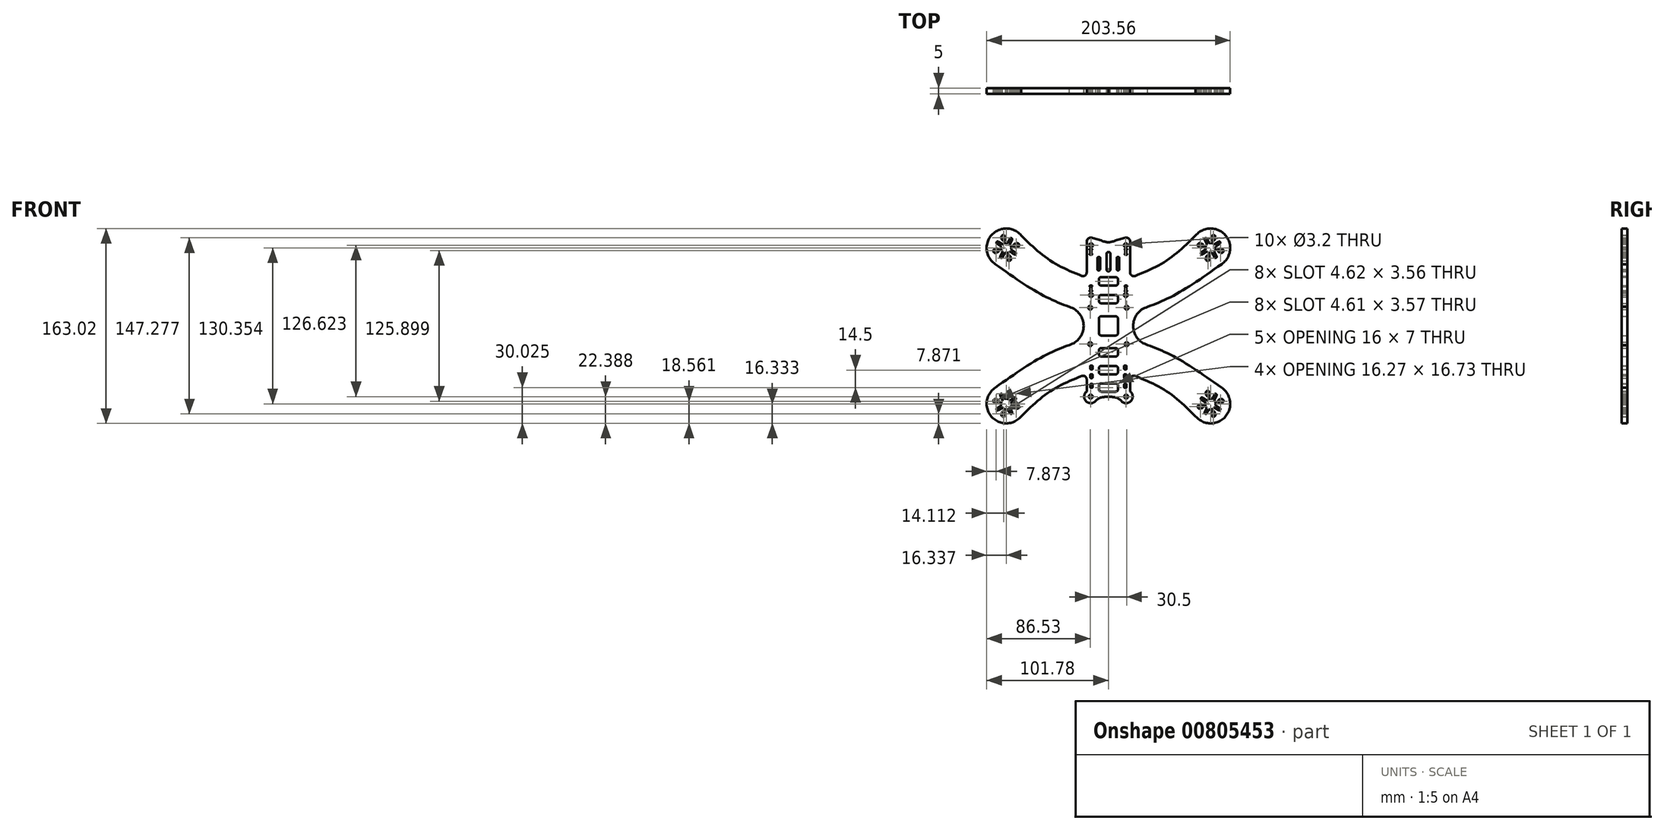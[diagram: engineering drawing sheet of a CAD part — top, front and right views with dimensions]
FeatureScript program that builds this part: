
annotation { "Feature Type Name" : "Feature", "Feature Type Description" : "" }
export const myFeature = defineFeature(function(context is Context, id is Id, definition is map)
    precondition{}
    {
        {
            var Q0;
            Q0=qCreatedBy(makeId("Front.planeOp"),FACE);
            var sketch = newSketch(context, id + "F0", { "sketchPlane" : qUnion([Q0])});
            skArc(sketch, "E0", {"start": v(-89.64, 66.06) * mm, "mid": v(-89.6, 64.08) * mm, "end": v(-88.66, 62.33) * mm});
            skLineSegment(sketch, "E1", {"start": v(0, 88.33) * mm, "end": v(0, -93.74) * mm, "construction": true});
            skPoint(sketch, "E2.startSnap0", {"position": v(-374.9, -63.32) * mm});
            skLineSegment(sketch, "E3.bottom", {"start": v(-6, 8) * mm, "end": v(6, 8) * mm});
            skLineSegment(sketch, "E3.top", {"start": v(-6, -8) * mm, "end": v(6, -8) * mm});
            skLineSegment(sketch, "E3.left", {"start": v(-8, 6) * mm, "end": v(-8, -6) * mm});
            skLineSegment(sketch, "E3.right", {"start": v(8, 6) * mm, "end": v(8, -6) * mm});
            skLineSegment(sketch, "E4", {"start": v(-85.44, 65.17) * mm, "end": v(85.13, -65.7) * mm, "construction": true});
            skCircle(sketch, "E5", {"center": v(85.13, -65.7) * mm, "radius": 4.25 * mm});
            skCircle(sketch, "E6.MirrorC", {"center": v(85.44, 65.17) * mm, "radius": 4.3 * mm});
            skCircle(sketch, "E7.MirrorC", {"center": v(-85.13, -65.7) * mm, "radius": 4.25 * mm});
            skLineSegment(sketch, "E8", {"start": v(-85.13, -65.7) * mm, "end": v(85.44, 65.17) * mm, "construction": true});
            skCircle(sketch, "E9", {"center": v(-15.25, 15.25) * mm, "radius": 1.6 * mm});
            skCircle(sketch, "E10.MirrorC", {"center": v(15.25, 15.25) * mm, "radius": 1.6 * mm});
            skCircle(sketch, "E11.MirrorC", {"center": v(-15.25, -15.25) * mm, "radius": 1.6 * mm});
            skCircle(sketch, "E12.MirrorC", {"center": v(15.25, -15.25) * mm, "radius": 1.6 * mm});
            skLineSegment(sketch, "E13", {"start": v(-42.21, 0) * mm, "end": v(44.56, 0) * mm, "construction": true});
            skArc(sketch, "E14", {"start": v(-72.93, 75.67) * mm, "mid": v(-97.56, 76.13) * mm, "end": v(-94.62, 51.67) * mm});
            skArc(sketch, "E15.MirrorC", {"start": v(72.93, 75.67) * mm, "mid": v(97.56, 76.13) * mm, "end": v(94.62, 51.67) * mm});
            skArc(sketch, "E16.MirrorC", {"start": v(-72.93, -75.67) * mm, "mid": v(-97.56, -76.13) * mm, "end": v(-94.62, -51.67) * mm});
            skArc(sketch, "E17.MirrorC", {"start": v(72.93, -75.67) * mm, "mid": v(97.56, -76.13) * mm, "end": v(94.62, -51.67) * mm});
            skLineSegment(sketch, "E18", {"start": v(-18.18, 44.65) * mm, "end": v(-18.18, 70.48) * mm});
            skLineSegment(sketch, "E19", {"start": v(-18.18, -44.65) * mm, "end": v(-18.18, -54.8) * mm});
            skArc(sketch, "E20", {"start": v(-18.18, -54.8) * mm, "mid": v(-18.83, -62.84) * mm, "end": v(-10.77, -62.88) * mm});
            skArc(sketch, "E21.MirrorC", {"start": v(18.18, -54.8) * mm, "mid": v(18.83, -62.84) * mm, "end": v(10.77, -62.88) * mm});
            skLineSegment(sketch, "E22.MirrorCS", {"start": v(18.18, -44.65) * mm, "end": v(18.18, -54.8) * mm});
            skFitSpline(sketch, "E23", {"points": [v(-72.93, 75.67) * mm, v(-47.95, 54.25) * mm, v(-18.18, 40.22) * mm], "startDerivative": vector(47.55, -46.42) * mm, "endDerivative": vector(61.29, -24.48) * mm});
            skFitSpline(sketch, "E24.MirrorCS", {"points": [v(72.93, 75.67) * mm, v(47.95, 54.25) * mm, v(18.18, 40.22) * mm], "startDerivative": vector(-47.55, -46.42) * mm, "endDerivative": vector(-61.29, -24.48) * mm});
            skFitSpline(sketch, "E25.MirrorCS", {"points": [v(-72.93, -75.67) * mm, v(-47.95, -54.25) * mm, v(-18.18, -40.22) * mm], "startDerivative": vector(47.55, 46.42) * mm, "endDerivative": vector(61.29, 24.48) * mm});
            skFitSpline(sketch, "E26.MirrorCS", {"points": [v(72.93, -75.67) * mm, v(47.95, -54.25) * mm, v(18.18, -40.22) * mm], "startDerivative": vector(-47.55, 46.42) * mm, "endDerivative": vector(-61.29, 24.48) * mm});
            skFitSpline(sketch, "E27", {"points": [v(-94.62, 51.67) * mm, v(-56.37, 26.47) * mm, v(-32.33, 15.78) * mm], "startDerivative": vector(71.34, -50.5) * mm, "endDerivative": vector(53.4, -20.59) * mm});
            skFitSpline(sketch, "E28.MirrorCS", {"points": [v(94.62, 51.67) * mm, v(56.37, 26.47) * mm, v(32.33, 15.78) * mm], "startDerivative": vector(-71.34, -50.5) * mm, "endDerivative": vector(-53.4, -20.59) * mm});
            skFitSpline(sketch, "E29.MirrorCS", {"points": [v(-94.62, -51.67) * mm, v(-56.37, -26.47) * mm, v(-32.33, -15.78) * mm], "startDerivative": vector(71.34, 50.5) * mm, "endDerivative": vector(53.4, 20.59) * mm});
            skFitSpline(sketch, "E30.MirrorCS", {"points": [v(94.62, -51.67) * mm, v(56.37, -26.47) * mm, v(32.33, -15.78) * mm], "startDerivative": vector(-71.34, 50.5) * mm, "endDerivative": vector(-53.4, 20.59) * mm});
            skPoint(sketch, "E31.orphan", {"position": v(-18.18, -38.8) * mm});
            skPoint(sketch, "E32.orphan", {"position": v(18.18, -38.8) * mm});
            skArc(sketch, "E33", {"start": v(-32.71, -15.93) * mm, "mid": v(-20.68, 0) * mm, "end": v(-32.71, 15.93) * mm});
            skArc(sketch, "E34.MirrorCS", {"start": v(32.71, -15.93) * mm, "mid": v(20.68, 0) * mm, "end": v(32.71, 15.93) * mm});
            skFitSpline(sketch, "E35", {"points": [v(-10.77, -62.88) * mm, v(-7.02, -60.12) * mm, v(0, -59.29) * mm], "startDerivative": vector(7.83, 7.8) * mm, "endDerivative": vector(14.08, 0.15) * mm});
            skFitSpline(sketch, "E36.MirrorCS", {"points": [v(10.77, -62.88) * mm, v(7.02, -60.12) * mm, v(0, -59.29) * mm], "startDerivative": vector(-7.83, 7.8) * mm, "endDerivative": vector(-14.08, 0.15) * mm});
            skPoint(sketch, "E37.orphan", {"position": v(-9.3, -59.45) * mm});
            skPoint(sketch, "E38.orphan", {"position": v(9.3, -59.45) * mm});
            skCircle(sketch, "E39", {"center": v(-14.78, -59.12) * mm, "radius": 1.6 * mm});
            skCircle(sketch, "E40.MirrorC", {"center": v(14.78, -59.12) * mm, "radius": 1.6 * mm});
            skCircle(sketch, "E41", {"center": v(-14.5, 25.75) * mm, "radius": 1.6 * mm});
            skCircle(sketch, "E42", {"center": v(-14.5, 67.5) * mm, "radius": 1.6 * mm});
            skCircle(sketch, "E43.MirrorC", {"center": v(14.5, 67.5) * mm, "radius": 1.6 * mm});
            skCircle(sketch, "E44.MirrorC", {"center": v(14.5, 25.75) * mm, "radius": 1.6 * mm});
            skArc(sketch, "E45.filletArc", {"start": v(-22.3, 41.86) * mm, "mid": v(-19.5, 42.16) * mm, "end": v(-18.18, 44.65) * mm});
            skPoint(sketch, "E46.newPointA", {"position": v(18.84, 40.22) * mm});
            skArc(sketch, "E47.filletArc", {"start": v(22.3, -41.86) * mm, "mid": v(19.5, -42.16) * mm, "end": v(18.18, -44.65) * mm});
            skArc(sketch, "E48.filletArc", {"start": v(-18.18, -44.65) * mm, "mid": v(-19.5, -42.16) * mm, "end": v(-22.3, -41.86) * mm});
            skLineSegment(sketch, "E49.MirrorCS", {"start": v(18.18, 44.65) * mm, "end": v(18.18, 70.48) * mm});
            skArc(sketch, "E50.MirrorCS", {"start": v(22.3, 41.86) * mm, "mid": v(19.5, 42.16) * mm, "end": v(18.18, 44.65) * mm});
            skPoint(sketch, "E51.orphan", {"position": v(-18.18, 74.02) * mm});
            skPoint(sketch, "E52.orphan", {"position": v(18.18, 74.02) * mm});
            skFitSpline(sketch, "E53", {"points": [v(-18.18, 71.17) * mm, v(-15.57, 73.68) * mm, v(-3.04, 70.45) * mm, v(0, 70.12) * mm], "startDerivative": vector(6.13, 13.03) * mm, "endDerivative": vector(9.34, 0.51) * mm});
            skArc(sketch, "E54.filletArc", {"start": v(-17.84, 71.88) * mm, "mid": v(-18.1, 71.2) * mm, "end": v(-18.18, 70.48) * mm});
            skFitSpline(sketch, "E55.MirrorCS", {"points": [v(18.18, 71.17) * mm, v(15.57, 73.68) * mm, v(3.04, 70.45) * mm, v(0, 70.12) * mm], "startDerivative": vector(-6.13, 13.03) * mm, "endDerivative": vector(-9.34, 0.51) * mm});
            skArc(sketch, "E56.MirrorCS", {"start": v(17.84, 71.88) * mm, "mid": v(18.1, 71.2) * mm, "end": v(18.18, 70.48) * mm});
            skPoint(sketch, "E57.visualSharp", {"position": v(-8, 8) * mm});
            skArc(sketch, "E57.filletArc", {"start": v(-6, 8) * mm, "mid": v(-7.41, 7.41) * mm, "end": v(-8, 6) * mm});
            skPoint(sketch, "E58.visualSharp", {"position": v(8, 8) * mm});
            skArc(sketch, "E58.filletArc", {"start": v(8, 6) * mm, "mid": v(7.41, 7.41) * mm, "end": v(6, 8) * mm});
            skPoint(sketch, "E59.visualSharp", {"position": v(8, -8) * mm});
            skArc(sketch, "E59.filletArc", {"start": v(6, -8) * mm, "mid": v(7.41, -7.41) * mm, "end": v(8, -6) * mm});
            skPoint(sketch, "E60.visualSharp", {"position": v(-8, -8) * mm});
            skArc(sketch, "E60.filletArc", {"start": v(-8, -6) * mm, "mid": v(-7.41, -7.41) * mm, "end": v(-6, -8) * mm});
            skLineSegment(sketch, "E61.bottom", {"start": v(-6, -18.58) * mm, "end": v(6, -18.58) * mm});
            skLineSegment(sketch, "E61.top", {"start": v(-6, -25.58) * mm, "end": v(6, -25.58) * mm});
            skLineSegment(sketch, "E61.left", {"start": v(-8, -20.58) * mm, "end": v(-8, -23.58) * mm});
            skLineSegment(sketch, "E61.right", {"start": v(8, -20.58) * mm, "end": v(8, -23.58) * mm});
            skPoint(sketch, "E62.visualSharp", {"position": v(-8, -18.58) * mm});
            skArc(sketch, "E62.filletArc", {"start": v(-6, -18.58) * mm, "mid": v(-7.41, -19.17) * mm, "end": v(-8, -20.58) * mm});
            skPoint(sketch, "E63.visualSharp", {"position": v(8, -18.58) * mm});
            skArc(sketch, "E63.filletArc", {"start": v(8, -20.58) * mm, "mid": v(7.41, -19.17) * mm, "end": v(6, -18.58) * mm});
            skPoint(sketch, "E64.visualSharp", {"position": v(8, -25.58) * mm});
            skArc(sketch, "E64.filletArc", {"start": v(6, -25.58) * mm, "mid": v(7.41, -25) * mm, "end": v(8, -23.58) * mm});
            skPoint(sketch, "E65.visualSharp", {"position": v(-8, -25.58) * mm});
            skArc(sketch, "E65.filletArc", {"start": v(-8, -23.58) * mm, "mid": v(-7.41, -25) * mm, "end": v(-6, -25.58) * mm});
            skLineSegment(sketch, "E66.bottom", {"start": v(-6, -33.49) * mm, "end": v(6, -33.49) * mm});
            skLineSegment(sketch, "E66.top", {"start": v(-6, -40.49) * mm, "end": v(6, -40.49) * mm});
            skLineSegment(sketch, "E66.left", {"start": v(-8, -35.49) * mm, "end": v(-8, -38.49) * mm});
            skLineSegment(sketch, "E66.right", {"start": v(8, -35.49) * mm, "end": v(8, -38.49) * mm});
            skPoint(sketch, "E67.visualSharp", {"position": v(-8, -33.49) * mm});
            skArc(sketch, "E67.filletArc", {"start": v(-6, -33.49) * mm, "mid": v(-7.41, -34.07) * mm, "end": v(-8, -35.49) * mm});
            skPoint(sketch, "E68.visualSharp", {"position": v(8, -33.49) * mm});
            skArc(sketch, "E68.filletArc", {"start": v(8, -35.49) * mm, "mid": v(7.41, -34.07) * mm, "end": v(6, -33.49) * mm});
            skPoint(sketch, "E69.visualSharp", {"position": v(8, -40.49) * mm});
            skArc(sketch, "E69.filletArc", {"start": v(6, -40.49) * mm, "mid": v(7.41, -39.9) * mm, "end": v(8, -38.49) * mm});
            skPoint(sketch, "E70.visualSharp", {"position": v(-8, -40.49) * mm});
            skArc(sketch, "E70.filletArc", {"start": v(-8, -38.49) * mm, "mid": v(-7.41, -39.9) * mm, "end": v(-6, -40.49) * mm});
            skLineSegment(sketch, "E71.bottom", {"start": v(-6, -47.99) * mm, "end": v(6, -47.99) * mm});
            skLineSegment(sketch, "E71.top", {"start": v(-6, -54.99) * mm, "end": v(6, -54.99) * mm});
            skLineSegment(sketch, "E71.left", {"start": v(-8, -49.99) * mm, "end": v(-8, -52.99) * mm});
            skLineSegment(sketch, "E71.right", {"start": v(8, -49.99) * mm, "end": v(8, -52.99) * mm});
            skPoint(sketch, "E72.visualSharp", {"position": v(-8, -47.99) * mm});
            skArc(sketch, "E72.filletArc", {"start": v(-6, -47.99) * mm, "mid": v(-7.41, -48.57) * mm, "end": v(-8, -49.99) * mm});
            skPoint(sketch, "E73.visualSharp", {"position": v(8, -47.99) * mm});
            skArc(sketch, "E73.filletArc", {"start": v(8, -49.99) * mm, "mid": v(7.41, -48.57) * mm, "end": v(6, -47.99) * mm});
            skPoint(sketch, "E74.visualSharp", {"position": v(8, -54.99) * mm});
            skArc(sketch, "E74.filletArc", {"start": v(6, -54.99) * mm, "mid": v(7.41, -54.4) * mm, "end": v(8, -52.99) * mm});
            skPoint(sketch, "E75.visualSharp", {"position": v(-8, -54.99) * mm});
            skArc(sketch, "E75.filletArc", {"start": v(-8, -52.99) * mm, "mid": v(-7.41, -54.4) * mm, "end": v(-6, -54.99) * mm});
            skLineSegment(sketch, "E76.bottom", {"start": v(-6, 25.92) * mm, "end": v(6, 25.92) * mm});
            skLineSegment(sketch, "E76.top", {"start": v(-6, 18.92) * mm, "end": v(6, 18.92) * mm});
            skLineSegment(sketch, "E76.left", {"start": v(-8, 23.92) * mm, "end": v(-8, 20.92) * mm});
            skLineSegment(sketch, "E76.right", {"start": v(8, 23.92) * mm, "end": v(8, 20.92) * mm});
            skPoint(sketch, "E77.visualSharp", {"position": v(-8, 25.92) * mm});
            skArc(sketch, "E77.filletArc", {"start": v(-6, 25.92) * mm, "mid": v(-7.41, 25.33) * mm, "end": v(-8, 23.92) * mm});
            skPoint(sketch, "E78.visualSharp", {"position": v(8, 25.92) * mm});
            skArc(sketch, "E78.filletArc", {"start": v(8, 23.92) * mm, "mid": v(7.41, 25.33) * mm, "end": v(6, 25.92) * mm});
            skPoint(sketch, "E79.visualSharp", {"position": v(8, 18.92) * mm});
            skArc(sketch, "E79.filletArc", {"start": v(6, 18.92) * mm, "mid": v(7.41, 19.5) * mm, "end": v(8, 20.92) * mm});
            skPoint(sketch, "E80.visualSharp", {"position": v(-8, 18.92) * mm});
            skArc(sketch, "E80.filletArc", {"start": v(-8, 20.92) * mm, "mid": v(-7.41, 19.5) * mm, "end": v(-6, 18.92) * mm});
            skLineSegment(sketch, "E81.bottom", {"start": v(-6, 40.78) * mm, "end": v(6, 40.78) * mm});
            skLineSegment(sketch, "E81.top", {"start": v(-6, 33.78) * mm, "end": v(6, 33.78) * mm});
            skLineSegment(sketch, "E81.left", {"start": v(-8, 38.78) * mm, "end": v(-8, 35.78) * mm});
            skLineSegment(sketch, "E81.right", {"start": v(8, 38.78) * mm, "end": v(8, 35.78) * mm});
            skPoint(sketch, "E82.visualSharp", {"position": v(-8, 40.78) * mm});
            skArc(sketch, "E82.filletArc", {"start": v(-6, 40.78) * mm, "mid": v(-7.41, 40.2) * mm, "end": v(-8, 38.78) * mm});
            skPoint(sketch, "E83.visualSharp", {"position": v(8, 40.78) * mm});
            skArc(sketch, "E83.filletArc", {"start": v(8, 38.78) * mm, "mid": v(7.41, 40.2) * mm, "end": v(6, 40.78) * mm});
            skPoint(sketch, "E84.visualSharp", {"position": v(8, 33.78) * mm});
            skArc(sketch, "E84.filletArc", {"start": v(6, 33.78) * mm, "mid": v(7.41, 34.37) * mm, "end": v(8, 35.78) * mm});
            skPoint(sketch, "E85.visualSharp", {"position": v(-8, 33.78) * mm});
            skArc(sketch, "E85.filletArc", {"start": v(-8, 35.78) * mm, "mid": v(-7.41, 34.37) * mm, "end": v(-6, 33.78) * mm});
            skLineSegment(sketch, "E86.bottom", {"start": v(-14.65, -33.17) * mm, "end": v(-13.65, -33.17) * mm});
            skLineSegment(sketch, "E86.top", {"start": v(-14.65, -36.37) * mm, "end": v(-13.65, -36.37) * mm});
            skLineSegment(sketch, "E86.left", {"start": v(-15.15, -33.67) * mm, "end": v(-15.15, -35.87) * mm});
            skLineSegment(sketch, "E86.right", {"start": v(-13.15, -33.67) * mm, "end": v(-13.15, -35.87) * mm});
            skPoint(sketch, "E87.visualSharp", {"position": v(-15.15, -33.17) * mm});
            skArc(sketch, "E87.filletArc", {"start": v(-14.65, -33.17) * mm, "mid": v(-15, -33.31) * mm, "end": v(-15.15, -33.67) * mm});
            skPoint(sketch, "E88.visualSharp", {"position": v(-13.15, -33.17) * mm});
            skArc(sketch, "E88.filletArc", {"start": v(-13.15, -33.67) * mm, "mid": v(-13.3, -33.31) * mm, "end": v(-13.65, -33.17) * mm});
            skPoint(sketch, "E89.visualSharp", {"position": v(-15.15, -36.37) * mm});
            skArc(sketch, "E89.filletArc", {"start": v(-15.15, -35.87) * mm, "mid": v(-15, -36.22) * mm, "end": v(-14.65, -36.37) * mm});
            skPoint(sketch, "E90.visualSharp", {"position": v(-13.15, -36.37) * mm});
            skArc(sketch, "E90.filletArc", {"start": v(-13.65, -36.37) * mm, "mid": v(-13.3, -36.22) * mm, "end": v(-13.15, -35.87) * mm});
            skLineSegment(sketch, "E91.bottom", {"start": v(-14.65, -40.37) * mm, "end": v(-13.65, -40.37) * mm});
            skLineSegment(sketch, "E91.top", {"start": v(-14.65, -43.57) * mm, "end": v(-13.65, -43.57) * mm});
            skLineSegment(sketch, "E91.left", {"start": v(-15.15, -40.87) * mm, "end": v(-15.15, -43.07) * mm});
            skLineSegment(sketch, "E91.right", {"start": v(-13.15, -40.87) * mm, "end": v(-13.15, -43.07) * mm});
            skPoint(sketch, "E92.visualSharp", {"position": v(-15.15, -40.37) * mm});
            skArc(sketch, "E92.filletArc", {"start": v(-14.65, -40.37) * mm, "mid": v(-15, -40.51) * mm, "end": v(-15.15, -40.87) * mm});
            skPoint(sketch, "E93.visualSharp", {"position": v(-13.15, -40.37) * mm});
            skArc(sketch, "E93.filletArc", {"start": v(-13.15, -40.87) * mm, "mid": v(-13.3, -40.51) * mm, "end": v(-13.65, -40.37) * mm});
            skPoint(sketch, "E94.visualSharp", {"position": v(-13.15, -43.57) * mm});
            skArc(sketch, "E94.filletArc", {"start": v(-13.65, -43.57) * mm, "mid": v(-13.3, -43.42) * mm, "end": v(-13.15, -43.07) * mm});
            skPoint(sketch, "E95.visualSharp", {"position": v(-15.15, -43.57) * mm});
            skArc(sketch, "E95.filletArc", {"start": v(-15.15, -43.07) * mm, "mid": v(-15, -43.42) * mm, "end": v(-14.65, -43.57) * mm});
            skLineSegment(sketch, "E96.bottom", {"start": v(-14.65, -48.57) * mm, "end": v(-13.65, -48.57) * mm});
            skLineSegment(sketch, "E96.top", {"start": v(-14.65, -51.77) * mm, "end": v(-13.65, -51.77) * mm});
            skLineSegment(sketch, "E96.left", {"start": v(-15.15, -49.07) * mm, "end": v(-15.15, -51.27) * mm});
            skLineSegment(sketch, "E96.right", {"start": v(-13.15, -49.07) * mm, "end": v(-13.15, -51.27) * mm});
            skPoint(sketch, "E97.visualSharp", {"position": v(-15.15, -48.57) * mm});
            skArc(sketch, "E97.filletArc", {"start": v(-14.65, -48.57) * mm, "mid": v(-15, -48.71) * mm, "end": v(-15.15, -49.07) * mm});
            skPoint(sketch, "E98.visualSharp", {"position": v(-13.15, -48.57) * mm});
            skArc(sketch, "E98.filletArc", {"start": v(-13.15, -49.07) * mm, "mid": v(-13.3, -48.71) * mm, "end": v(-13.65, -48.57) * mm});
            skPoint(sketch, "E99.visualSharp", {"position": v(-13.15, -51.77) * mm});
            skArc(sketch, "E99.filletArc", {"start": v(-13.65, -51.77) * mm, "mid": v(-13.3, -51.62) * mm, "end": v(-13.15, -51.27) * mm});
            skPoint(sketch, "E100.visualSharp", {"position": v(-15.15, -51.77) * mm});
            skArc(sketch, "E100.filletArc", {"start": v(-15.15, -51.27) * mm, "mid": v(-15, -51.62) * mm, "end": v(-14.65, -51.77) * mm});
            skLineSegment(sketch, "E101.MirrorCS", {"start": v(14.65, -51.77) * mm, "end": v(13.65, -51.77) * mm});
            skLineSegment(sketch, "E102.MirrorCS", {"start": v(14.65, -36.37) * mm, "end": v(13.65, -36.37) * mm});
            skArc(sketch, "E103.MirrorCS", {"start": v(13.65, -36.37) * mm, "mid": v(13.3, -36.22) * mm, "end": v(13.15, -35.87) * mm});
            skArc(sketch, "E104.MirrorCS", {"start": v(13.15, -40.87) * mm, "mid": v(13.3, -40.51) * mm, "end": v(13.65, -40.37) * mm});
            skLineSegment(sketch, "E105.MirrorCS", {"start": v(14.65, -40.37) * mm, "end": v(13.65, -40.37) * mm});
            skLineSegment(sketch, "E106.MirrorCS", {"start": v(13.15, -40.87) * mm, "end": v(13.15, -43.07) * mm});
            skArc(sketch, "E107.MirrorCS", {"start": v(15.15, -51.27) * mm, "mid": v(15, -51.62) * mm, "end": v(14.65, -51.77) * mm});
            skArc(sketch, "E108.MirrorCS", {"start": v(13.65, -43.57) * mm, "mid": v(13.3, -43.42) * mm, "end": v(13.15, -43.07) * mm});
            skArc(sketch, "E109.MirrorCS", {"start": v(14.65, -40.37) * mm, "mid": v(15, -40.51) * mm, "end": v(15.15, -40.87) * mm});
            skLineSegment(sketch, "E110.MirrorCS", {"start": v(14.65, -43.57) * mm, "end": v(13.65, -43.57) * mm});
            skLineSegment(sketch, "E111.MirrorCS", {"start": v(13.15, -49.07) * mm, "end": v(13.15, -51.27) * mm});
            skArc(sketch, "E112.MirrorCS", {"start": v(13.15, -49.07) * mm, "mid": v(13.3, -48.71) * mm, "end": v(13.65, -48.57) * mm});
            skLineSegment(sketch, "E113.MirrorCS", {"start": v(13.15, -33.67) * mm, "end": v(13.15, -35.87) * mm});
            skArc(sketch, "E114.MirrorCS", {"start": v(13.15, -33.67) * mm, "mid": v(13.3, -33.31) * mm, "end": v(13.65, -33.17) * mm});
            skLineSegment(sketch, "E115.MirrorCS", {"start": v(15.15, -49.07) * mm, "end": v(15.15, -51.27) * mm});
            skLineSegment(sketch, "E116.MirrorCS", {"start": v(15.15, -40.87) * mm, "end": v(15.15, -43.07) * mm});
            skLineSegment(sketch, "E117.MirrorCS", {"start": v(14.65, -48.57) * mm, "end": v(13.65, -48.57) * mm});
            skArc(sketch, "E118.MirrorCS", {"start": v(15.15, -43.07) * mm, "mid": v(15, -43.42) * mm, "end": v(14.65, -43.57) * mm});
            skLineSegment(sketch, "E119.MirrorCS", {"start": v(14.65, -33.17) * mm, "end": v(13.65, -33.17) * mm});
            skLineSegment(sketch, "E120.MirrorCS", {"start": v(15.15, -33.67) * mm, "end": v(15.15, -35.87) * mm});
            skArc(sketch, "E121.MirrorCS", {"start": v(14.65, -33.17) * mm, "mid": v(15, -33.31) * mm, "end": v(15.15, -33.67) * mm});
            skArc(sketch, "E122.MirrorCS", {"start": v(15.15, -35.87) * mm, "mid": v(15, -36.22) * mm, "end": v(14.65, -36.37) * mm});
            skArc(sketch, "E123.MirrorCS", {"start": v(13.65, -51.77) * mm, "mid": v(13.3, -51.62) * mm, "end": v(13.15, -51.27) * mm});
            skArc(sketch, "E124.MirrorCS", {"start": v(14.65, -48.57) * mm, "mid": v(15, -48.71) * mm, "end": v(15.15, -49.07) * mm});
            skPoint(sketch, "E125.MirrorP", {"position": v(15.15, -51.77) * mm});
            skPoint(sketch, "E126.MirrorP", {"position": v(15.15, -40.37) * mm});
            skPoint(sketch, "E127.MirrorP", {"position": v(13.15, -36.37) * mm});
            skPoint(sketch, "E128.MirrorP", {"position": v(13.15, -51.77) * mm});
            skPoint(sketch, "E129.MirrorP", {"position": v(15.15, -43.57) * mm});
            skPoint(sketch, "E130.MirrorP", {"position": v(13.15, -48.57) * mm});
            skPoint(sketch, "E131.MirrorP", {"position": v(15.15, -36.37) * mm});
            skPoint(sketch, "E132.MirrorP", {"position": v(13.15, -40.37) * mm});
            skPoint(sketch, "E133.MirrorP", {"position": v(13.15, -33.17) * mm});
            skPoint(sketch, "E134.MirrorP", {"position": v(15.15, -33.17) * mm});
            skPoint(sketch, "E135.MirrorP", {"position": v(15.15, -48.57) * mm});
            skPoint(sketch, "E136.MirrorP", {"position": v(13.15, -43.57) * mm});
            skLineSegment(sketch, "E137", {"start": v(1.6, 53.73) * mm, "end": v(1.6, 53.73) * mm});
            skArc(sketch, "E138", {"start": v(-1.6, 47.27) * mm, "mid": v(-0.01, 45.65) * mm, "end": v(1.6, 47.25) * mm});
            skLineSegment(sketch, "E139", {"start": v(1.6, 53.73) * mm, "end": v(1.6, 47.25) * mm});
            skLineSegment(sketch, "E140", {"start": v(-1.6, 53.73) * mm, "end": v(-1.6, 47.27) * mm});
            skLineSegment(sketch, "E141.bottom", {"start": v(-8.55, 46.6) * mm, "end": v(-7.55, 46.6) * mm});
            skLineSegment(sketch, "E141.top", {"start": v(-8.55, 57.6) * mm, "end": v(-7.55, 57.6) * mm});
            skLineSegment(sketch, "E141.left", {"start": v(-9.05, 47.1) * mm, "end": v(-9.05, 57.1) * mm});
            skLineSegment(sketch, "E141.right", {"start": v(-7.05, 47.1) * mm, "end": v(-7.05, 57.1) * mm});
            skPoint(sketch, "E142.visualSharp", {"position": v(-9.05, 57.6) * mm});
            skArc(sketch, "E142.filletArc", {"start": v(-8.55, 57.6) * mm, "mid": v(-8.9, 57.45) * mm, "end": v(-9.05, 57.1) * mm});
            skPoint(sketch, "E143.visualSharp", {"position": v(-7.05, 57.6) * mm});
            skArc(sketch, "E143.filletArc", {"start": v(-7.05, 57.1) * mm, "mid": v(-7.2, 57.45) * mm, "end": v(-7.55, 57.6) * mm});
            skPoint(sketch, "E144.visualSharp", {"position": v(-7.05, 46.6) * mm});
            skArc(sketch, "E144.filletArc", {"start": v(-7.55, 46.6) * mm, "mid": v(-7.2, 46.74) * mm, "end": v(-7.05, 47.1) * mm});
            skPoint(sketch, "E145.visualSharp", {"position": v(-9.05, 46.6) * mm});
            skArc(sketch, "E145.filletArc", {"start": v(-9.05, 47.1) * mm, "mid": v(-8.9, 46.74) * mm, "end": v(-8.55, 46.6) * mm});
            skLineSegment(sketch, "E146.MirrorCS", {"start": v(8.55, 57.6) * mm, "end": v(7.55, 57.6) * mm});
            skArc(sketch, "E147.MirrorCS", {"start": v(8.55, 57.6) * mm, "mid": v(8.9, 57.45) * mm, "end": v(9.05, 57.1) * mm});
            skArc(sketch, "E148.MirrorCS", {"start": v(7.05, 57.1) * mm, "mid": v(7.2, 57.45) * mm, "end": v(7.55, 57.6) * mm});
            skLineSegment(sketch, "E149.MirrorCS", {"start": v(7.05, 47.1) * mm, "end": v(7.05, 57.1) * mm});
            skLineSegment(sketch, "E150.MirrorCS", {"start": v(9.05, 47.1) * mm, "end": v(9.05, 57.1) * mm});
            skArc(sketch, "E151.MirrorCS", {"start": v(9.05, 47.1) * mm, "mid": v(8.9, 46.74) * mm, "end": v(8.55, 46.6) * mm});
            skLineSegment(sketch, "E152.MirrorCS", {"start": v(8.55, 46.6) * mm, "end": v(7.55, 46.6) * mm});
            skArc(sketch, "E153.MirrorCS", {"start": v(7.55, 46.6) * mm, "mid": v(7.2, 46.74) * mm, "end": v(7.05, 47.1) * mm});
            skArc(sketch, "E154", {"start": v(1.6, 60.25) * mm, "mid": v(0, 61.85) * mm, "end": v(-1.6, 60.25) * mm});
            skLineSegment(sketch, "E155", {"start": v(1.6, 60.25) * mm, "end": v(1.6, 53.73) * mm});
            skLineSegment(sketch, "E156.MirrorCS", {"start": v(-1.6, 60.25) * mm, "end": v(-1.6, 53.73) * mm});
            skLineSegment(sketch, "E157.trimOffspring", {"start": v(-1.6, 53.73) * mm, "end": v(-1.6, 53.73) * mm});
            skCircle(sketch, "E158", {"center": v(-85.44, 65.17) * mm, "radius": 9.5 * mm, "construction": true});
            skCircle(sketch, "E159", {"center": v(-85.44, 65.17) * mm, "radius": 8 * mm, "construction": true});
            skLineSegment(sketch, "E160", {"start": v(-85.44, 77.56) * mm, "end": v(-85.44, 52.95) * mm, "construction": true});
            skLineSegment(sketch, "E161", {"start": v(-96.43, 65.17) * mm, "end": v(-73.79, 65.17) * mm, "construction": true});
            skLineSegment(sketch, "E162", {"start": v(-81.38, 49.77) * mm, "end": v(-88.78, 77.85) * mm, "construction": true});
            skLineSegment(sketch, "E163", {"start": v(-99.15, 61.56) * mm, "end": v(-72.27, 68.65) * mm, "construction": true});
            skArc(sketch, "E164", {"start": v(-89.06, 72.65) * mm, "mid": v(-87.07, 71.36) * mm, "end": v(-85.98, 73.46) * mm});
            skLineSegment(sketch, "E165", {"start": v(-89.06, 72.65) * mm, "end": v(-89.4, 73.95) * mm});
            skLineSegment(sketch, "E166.MirrorCS", {"start": v(-85.98, 73.46) * mm, "end": v(-86.31, 74.76) * mm});
            skArc(sketch, "E167.trimOffspring", {"start": v(-86.31, 74.76) * mm, "mid": v(-88.27, 75.9) * mm, "end": v(-89.4, 73.95) * mm});
            skLineSegment(sketch, "E168", {"start": v(-21.7, 46.63) * mm, "end": v(20.3, 46.63) * mm, "construction": true});
            skPoint(sketch, "E169.MirrorP", {"position": v(18.18, 19.25) * mm});
            skPoint(sketch, "E170.MirrorP", {"position": v(18.18, 22.1) * mm});
            skPoint(sketch, "E171.MirrorP", {"position": v(-18.18, 22.1) * mm});
            skPoint(sketch, "E172.MirrorP", {"position": v(-18.18, 19.25) * mm});
            skArc(sketch, "E173.MirrorCS", {"start": v(-81.48, 56.4) * mm, "mid": v(-82.61, 54.44) * mm, "end": v(-84.57, 55.59) * mm});
            skLineSegment(sketch, "E174.MirrorCS", {"start": v(-84.9, 56.9) * mm, "end": v(-84.57, 55.59) * mm});
            skArc(sketch, "E175.MirrorCS", {"start": v(-84.9, 56.9) * mm, "mid": v(-83.81, 58.99) * mm, "end": v(-81.83, 57.7) * mm});
            skLineSegment(sketch, "E176.MirrorCS", {"start": v(-81.83, 57.7) * mm, "end": v(-81.48, 56.4) * mm});
            skArc(sketch, "E177", {"start": v(-92.94, 61.55) * mm, "mid": v(-91.63, 63.54) * mm, "end": v(-93.75, 64.63) * mm});
            skArc(sketch, "E178", {"start": v(-95, 64.31) * mm, "mid": v(-96.18, 62.35) * mm, "end": v(-94.18, 61.22) * mm});
            skLineSegment(sketch, "E179", {"start": v(-95, 64.31) * mm, "end": v(-93.75, 64.63) * mm});
            skLineSegment(sketch, "E180.MirrorCS", {"start": v(-94.18, 61.22) * mm, "end": v(-92.94, 61.55) * mm});
            skArc(sketch, "E181.MirrorCS", {"start": v(-77.13, 65.72) * mm, "mid": v(-79.25, 66.8) * mm, "end": v(-77.95, 68.8) * mm});
            skLineSegment(sketch, "E182.MirrorCS", {"start": v(-76.7, 69.13) * mm, "end": v(-77.95, 68.8) * mm});
            skLineSegment(sketch, "E183.MirrorCS", {"start": v(-75.9, 66.04) * mm, "end": v(-77.13, 65.72) * mm});
            skArc(sketch, "E184.MirrorCS", {"start": v(-76.7, 69.13) * mm, "mid": v(-74.7, 68) * mm, "end": v(-75.9, 66.04) * mm});
            skArc(sketch, "E185", {"start": v(-92.03, 70.42) * mm, "mid": v(-93.44, 70.12) * mm, "end": v(-93.08, 68.72) * mm});
            skArc(sketch, "E186.MirrorC", {"start": v(-82.3, 72.99) * mm, "mid": v(-80.99, 73.45) * mm, "end": v(-80.48, 72.16) * mm});
            skArc(sketch, "E187.MirrorC", {"start": v(-88.6, 57.36) * mm, "mid": v(-89.97, 56.93) * mm, "end": v(-90.34, 58.33) * mm});
            skArc(sketch, "E188.MirrorC", {"start": v(-78.85, 59.93) * mm, "mid": v(-77.49, 60.17) * mm, "end": v(-77.68, 61.54) * mm});
            skLineSegment(sketch, "E189", {"start": v(-93.08, 68.72) * mm, "end": v(-89.86, 66.58) * mm});
            skLineSegment(sketch, "E190", {"start": v(-92.03, 70.42) * mm, "end": v(-88.91, 68.33) * mm});
            skLineSegment(sketch, "E191.MirrorCS", {"start": v(-82.3, 72.99) * mm, "end": v(-83.98, 69.63) * mm});
            skLineSegment(sketch, "E192.MirrorCS", {"start": v(-80.48, 72.16) * mm, "end": v(-82.3, 68.57) * mm});
            skLineSegment(sketch, "E193.MirrorCS", {"start": v(-90.34, 58.33) * mm, "end": v(-88.59, 61.78) * mm});
            skLineSegment(sketch, "E194.MirrorCS", {"start": v(-88.6, 57.36) * mm, "end": v(-86.9, 60.72) * mm});
            skLineSegment(sketch, "E195.MirrorCS", {"start": v(-78.85, 59.93) * mm, "end": v(-81.97, 62.02) * mm});
            skLineSegment(sketch, "E196.MirrorCS", {"start": v(-77.68, 61.54) * mm, "end": v(-81.03, 63.77) * mm});
            skPoint(sketch, "E197.orphan", {"position": v(-93.2, 68.8) * mm});
            skArc(sketch, "E198.trimOffspring", {"start": v(-84.53, 69.37) * mm, "mid": v(-86.54, 69.33) * mm, "end": v(-88.3, 68.38) * mm});
            skArc(sketch, "E199.trimOffspring", {"start": v(-81.24, 64.29) * mm, "mid": v(-81.3, 66.27) * mm, "end": v(-82.23, 68.02) * mm});
            skArc(sketch, "E200.trimOffspring", {"start": v(-86.35, 60.98) * mm, "mid": v(-84.35, 61.02) * mm, "end": v(-82.58, 61.97) * mm});
            skPoint(sketch, "E201.orphan", {"position": v(-90.4, 58.19) * mm});
            skPoint(sketch, "E202.visualSharp", {"position": v(-84.16, 69.27) * mm});
            skArc(sketch, "E202.filletArc", {"start": v(-84.53, 69.37) * mm, "mid": v(-84.21, 69.4) * mm, "end": v(-83.98, 69.63) * mm});
            skPoint(sketch, "E203.visualSharp", {"position": v(-88.58, 68.1) * mm});
            skArc(sketch, "E203.filletArc", {"start": v(-88.91, 68.33) * mm, "mid": v(-88.6, 68.25) * mm, "end": v(-88.3, 68.38) * mm});
            skPoint(sketch, "E204.visualSharp", {"position": v(-89.56, 66.39) * mm});
            skArc(sketch, "E204.filletArc", {"start": v(-89.64, 66.06) * mm, "mid": v(-89.67, 66.35) * mm, "end": v(-89.86, 66.58) * mm});
            skPoint(sketch, "E205.visualSharp", {"position": v(-88.43, 62.1) * mm});
            skArc(sketch, "E205.filletArc", {"start": v(-88.59, 61.78) * mm, "mid": v(-88.54, 62.07) * mm, "end": v(-88.66, 62.33) * mm});
            skPoint(sketch, "E206.visualSharp", {"position": v(-86.73, 61.08) * mm});
            skArc(sketch, "E206.filletArc", {"start": v(-86.35, 60.98) * mm, "mid": v(-86.68, 60.94) * mm, "end": v(-86.9, 60.72) * mm});
            skPoint(sketch, "E207.visualSharp", {"position": v(-82.3, 62.24) * mm});
            skArc(sketch, "E207.filletArc", {"start": v(-81.97, 62.02) * mm, "mid": v(-82.29, 62.1) * mm, "end": v(-82.58, 61.97) * mm});
            skPoint(sketch, "E208.visualSharp", {"position": v(-81.33, 63.96) * mm});
            skArc(sketch, "E208.filletArc", {"start": v(-81.24, 64.29) * mm, "mid": v(-81.22, 64) * mm, "end": v(-81.03, 63.77) * mm});
            skPoint(sketch, "E209.visualSharp", {"position": v(-82.46, 68.26) * mm});
            skArc(sketch, "E209.filletArc", {"start": v(-82.3, 68.57) * mm, "mid": v(-82.35, 68.28) * mm, "end": v(-82.23, 68.02) * mm});
            skLineSegment(sketch, "E210.MirrorCS", {"start": v(85.98, 73.46) * mm, "end": v(86.31, 74.76) * mm});
            skLineSegment(sketch, "E211.MirrorCS", {"start": v(89.06, 72.65) * mm, "end": v(89.4, 73.95) * mm});
            skLineSegment(sketch, "E212.MirrorCS", {"start": v(94.18, 61.22) * mm, "end": v(92.94, 61.55) * mm});
            skArc(sketch, "E213.MirrorCS", {"start": v(81.24, 64.29) * mm, "mid": v(81.22, 64) * mm, "end": v(81.03, 63.77) * mm});
            skLineSegment(sketch, "E214.MirrorCS", {"start": v(95, 64.31) * mm, "end": v(93.75, 64.63) * mm});
            skArc(sketch, "E215.MirrorCS", {"start": v(89.64, 66.06) * mm, "mid": v(89.67, 66.35) * mm, "end": v(89.86, 66.58) * mm});
            skArc(sketch, "E216.MirrorCS", {"start": v(86.35, 60.98) * mm, "mid": v(84.35, 61.02) * mm, "end": v(82.58, 61.97) * mm});
            skArc(sketch, "E217.MirrorCS", {"start": v(84.53, 69.37) * mm, "mid": v(84.21, 69.4) * mm, "end": v(83.98, 69.63) * mm});
            skArc(sketch, "E218.MirrorCS", {"start": v(88.91, 68.33) * mm, "mid": v(88.6, 68.25) * mm, "end": v(88.3, 68.38) * mm});
            skArc(sketch, "E219.MirrorCS", {"start": v(88.59, 61.78) * mm, "mid": v(88.54, 62.07) * mm, "end": v(88.66, 62.33) * mm});
            skArc(sketch, "E220.MirrorCS", {"start": v(82.3, 68.57) * mm, "mid": v(82.35, 68.28) * mm, "end": v(82.23, 68.02) * mm});
            skArc(sketch, "E221.MirrorCS", {"start": v(86.35, 60.98) * mm, "mid": v(86.68, 60.94) * mm, "end": v(86.9, 60.72) * mm});
            skArc(sketch, "E222.MirrorCS", {"start": v(81.97, 62.02) * mm, "mid": v(82.29, 62.1) * mm, "end": v(82.58, 61.97) * mm});
            skLineSegment(sketch, "E223.MirrorCS", {"start": v(77.68, 61.54) * mm, "end": v(81.03, 63.77) * mm});
            skLineSegment(sketch, "E224.MirrorCS", {"start": v(78.85, 59.93) * mm, "end": v(81.97, 62.02) * mm});
            skLineSegment(sketch, "E225.MirrorCS", {"start": v(81.83, 57.7) * mm, "end": v(81.48, 56.4) * mm});
            skLineSegment(sketch, "E226.MirrorCS", {"start": v(80.48, 72.16) * mm, "end": v(82.3, 68.57) * mm});
            skLineSegment(sketch, "E227.MirrorCS", {"start": v(92.03, 70.42) * mm, "end": v(88.91, 68.33) * mm});
            skLineSegment(sketch, "E228.MirrorCS", {"start": v(88.6, 57.36) * mm, "end": v(86.9, 60.72) * mm});
            skArc(sketch, "E229.MirrorCS", {"start": v(89.64, 66.06) * mm, "mid": v(89.6, 64.08) * mm, "end": v(88.66, 62.33) * mm});
            skLineSegment(sketch, "E230.MirrorCS", {"start": v(76.7, 69.13) * mm, "end": v(77.95, 68.8) * mm});
            skArc(sketch, "E231.MirrorCS", {"start": v(89.06, 72.65) * mm, "mid": v(87.07, 71.36) * mm, "end": v(85.98, 73.46) * mm});
            skLineSegment(sketch, "E232.MirrorCS", {"start": v(82.3, 72.99) * mm, "end": v(83.98, 69.63) * mm});
            skLineSegment(sketch, "E233.MirrorCS", {"start": v(84.9, 56.9) * mm, "end": v(84.57, 55.59) * mm});
            skLineSegment(sketch, "E234.MirrorCS", {"start": v(90.34, 58.33) * mm, "end": v(88.59, 61.78) * mm});
            skLineSegment(sketch, "E235.MirrorCS", {"start": v(75.9, 66.04) * mm, "end": v(77.13, 65.72) * mm});
            skArc(sketch, "E236.MirrorCS", {"start": v(92.03, 70.42) * mm, "mid": v(93.44, 70.12) * mm, "end": v(93.08, 68.72) * mm});
            skArc(sketch, "E237.MirrorCS", {"start": v(84.53, 69.37) * mm, "mid": v(86.54, 69.33) * mm, "end": v(88.3, 68.38) * mm});
            skArc(sketch, "E238.MirrorCS", {"start": v(88.6, 57.36) * mm, "mid": v(89.97, 56.93) * mm, "end": v(90.34, 58.33) * mm});
            skArc(sketch, "E239.MirrorCS", {"start": v(78.85, 59.93) * mm, "mid": v(77.49, 60.17) * mm, "end": v(77.68, 61.54) * mm});
            skLineSegment(sketch, "E240.MirrorCS", {"start": v(93.08, 68.72) * mm, "end": v(89.86, 66.58) * mm});
            skArc(sketch, "E241.MirrorCS", {"start": v(82.3, 72.99) * mm, "mid": v(80.99, 73.45) * mm, "end": v(80.48, 72.16) * mm});
            skPoint(sketch, "E242.MirrorP", {"position": v(89.56, 66.39) * mm});
            skArc(sketch, "E243.MirrorCS", {"start": v(95, 64.31) * mm, "mid": v(96.18, 62.35) * mm, "end": v(94.18, 61.22) * mm});
            skArc(sketch, "E244.MirrorCS", {"start": v(86.31, 74.76) * mm, "mid": v(88.27, 75.9) * mm, "end": v(89.4, 73.95) * mm});
            skPoint(sketch, "E245.MirrorP", {"position": v(88.58, 68.1) * mm});
            skArc(sketch, "E246.MirrorCS", {"start": v(84.9, 56.9) * mm, "mid": v(83.81, 58.99) * mm, "end": v(81.83, 57.7) * mm});
            skArc(sketch, "E247.MirrorCS", {"start": v(81.24, 64.29) * mm, "mid": v(81.3, 66.27) * mm, "end": v(82.23, 68.02) * mm});
            skPoint(sketch, "E248.MirrorP", {"position": v(86.73, 61.08) * mm});
            skArc(sketch, "E249.MirrorCS", {"start": v(92.94, 61.55) * mm, "mid": v(91.63, 63.54) * mm, "end": v(93.75, 64.63) * mm});
            skArc(sketch, "E250.MirrorCS", {"start": v(77.13, 65.72) * mm, "mid": v(79.25, 66.8) * mm, "end": v(77.95, 68.8) * mm});
            skPoint(sketch, "E251.MirrorP", {"position": v(88.43, 62.1) * mm});
            skPoint(sketch, "E252.MirrorP", {"position": v(82.3, 62.24) * mm});
            skLineSegment(sketch, "E253.MirrorCS", {"start": v(96.43, 65.17) * mm, "end": v(73.79, 65.17) * mm, "construction": true});
            skArc(sketch, "E254.MirrorCS", {"start": v(81.48, 56.4) * mm, "mid": v(82.61, 54.44) * mm, "end": v(84.57, 55.59) * mm});
            skLineSegment(sketch, "E255.MirrorCS", {"start": v(85.44, 77.56) * mm, "end": v(85.44, 52.95) * mm, "construction": true});
            skPoint(sketch, "E256.MirrorP", {"position": v(81.33, 63.96) * mm});
            skPoint(sketch, "E257.MirrorP", {"position": v(84.16, 69.27) * mm});
            skCircle(sketch, "E258.MirrorC", {"center": v(85.44, 65.17) * mm, "radius": 9.5 * mm, "construction": true});
            skArc(sketch, "E259.MirrorCS", {"start": v(76.7, 69.13) * mm, "mid": v(74.7, 68) * mm, "end": v(75.9, 66.04) * mm});
            skLineSegment(sketch, "E260.MirrorCS", {"start": v(81.38, 49.77) * mm, "end": v(88.78, 77.85) * mm, "construction": true});
            skPoint(sketch, "E261.MirrorP", {"position": v(90.4, 58.19) * mm});
            skLineSegment(sketch, "E262.MirrorCS", {"start": v(99.15, 61.56) * mm, "end": v(72.27, 68.65) * mm, "construction": true});
            skPoint(sketch, "E263.MirrorP", {"position": v(82.46, 68.26) * mm});
            skCircle(sketch, "E264.MirrorC", {"center": v(85.44, 65.17) * mm, "radius": 8 * mm, "construction": true});
            skPoint(sketch, "E265.MirrorP", {"position": v(93.2, 68.8) * mm});
            skArc(sketch, "E266.MirrorCS", {"start": v(-88.91, -68.33) * mm, "mid": v(-88.6, -68.25) * mm, "end": v(-88.3, -68.38) * mm});
            skArc(sketch, "E267.MirrorCS", {"start": v(-84.53, -69.37) * mm, "mid": v(-84.21, -69.4) * mm, "end": v(-83.98, -69.63) * mm});
            skArc(sketch, "E268.MirrorCS", {"start": v(-89.64, -66.06) * mm, "mid": v(-89.67, -66.35) * mm, "end": v(-89.86, -66.58) * mm});
            skArc(sketch, "E269.MirrorCS", {"start": v(-89.64, -66.06) * mm, "mid": v(-89.6, -64.08) * mm, "end": v(-88.66, -62.33) * mm});
            skLineSegment(sketch, "E270.MirrorCS", {"start": v(-94.18, -61.22) * mm, "end": v(-92.94, -61.55) * mm});
            skArc(sketch, "E271.MirrorCS", {"start": v(-81.24, -64.29) * mm, "mid": v(-81.3, -66.27) * mm, "end": v(-82.23, -68.02) * mm});
            skLineSegment(sketch, "E272.MirrorCS", {"start": v(-89.06, -72.65) * mm, "end": v(-89.4, -73.95) * mm});
            skLineSegment(sketch, "E273.MirrorCS", {"start": v(-76.7, -69.13) * mm, "end": v(-77.95, -68.8) * mm});
            skArc(sketch, "E274.MirrorCS", {"start": v(-84.53, -69.37) * mm, "mid": v(-86.54, -69.33) * mm, "end": v(-88.3, -68.38) * mm});
            skArc(sketch, "E275.MirrorCS", {"start": v(-82.3, -68.57) * mm, "mid": v(-82.35, -68.28) * mm, "end": v(-82.23, -68.02) * mm});
            skArc(sketch, "E276.MirrorCS", {"start": v(-86.35, -60.98) * mm, "mid": v(-84.35, -61.02) * mm, "end": v(-82.58, -61.97) * mm});
            skArc(sketch, "E277.MirrorCS", {"start": v(-88.59, -61.78) * mm, "mid": v(-88.54, -62.07) * mm, "end": v(-88.66, -62.33) * mm});
            skArc(sketch, "E278.MirrorCS", {"start": v(-81.24, -64.29) * mm, "mid": v(-81.22, -64) * mm, "end": v(-81.03, -63.77) * mm});
            skArc(sketch, "E279.MirrorCS", {"start": v(-81.97, -62.02) * mm, "mid": v(-82.29, -62.1) * mm, "end": v(-82.58, -61.97) * mm});
            skArc(sketch, "E280.MirrorCS", {"start": v(-86.35, -60.98) * mm, "mid": v(-86.68, -60.94) * mm, "end": v(-86.9, -60.72) * mm});
            skLineSegment(sketch, "E281.MirrorCS", {"start": v(-95, -64.31) * mm, "end": v(-93.75, -64.63) * mm});
            skLineSegment(sketch, "E282.MirrorCS", {"start": v(-81.83, -57.7) * mm, "end": v(-81.48, -56.4) * mm});
            skLineSegment(sketch, "E283.MirrorCS", {"start": v(-78.85, -59.93) * mm, "end": v(-81.97, -62.02) * mm});
            skLineSegment(sketch, "E284.MirrorCS", {"start": v(-85.98, -73.46) * mm, "end": v(-86.31, -74.76) * mm});
            skLineSegment(sketch, "E285.MirrorCS", {"start": v(-88.6, -57.36) * mm, "end": v(-86.9, -60.72) * mm});
            skLineSegment(sketch, "E286.MirrorCS", {"start": v(-77.68, -61.54) * mm, "end": v(-81.03, -63.77) * mm});
            skLineSegment(sketch, "E287.MirrorCS", {"start": v(-75.9, -66.04) * mm, "end": v(-77.13, -65.72) * mm});
            skPoint(sketch, "E288.MirrorP", {"position": v(-82.3, -62.24) * mm});
            skLineSegment(sketch, "E289.MirrorCS", {"start": v(-82.3, -72.99) * mm, "end": v(-83.98, -69.63) * mm});
            skArc(sketch, "E290.MirrorCS", {"start": v(-86.31, -74.76) * mm, "mid": v(-88.27, -75.9) * mm, "end": v(-89.4, -73.95) * mm});
            skArc(sketch, "E291.MirrorCS", {"start": v(-95, -64.31) * mm, "mid": v(-96.18, -62.35) * mm, "end": v(-94.18, -61.22) * mm});
            skArc(sketch, "E292.MirrorCS", {"start": v(-84.9, -56.9) * mm, "mid": v(-83.81, -58.99) * mm, "end": v(-81.83, -57.7) * mm});
            skArc(sketch, "E293.MirrorCS", {"start": v(-92.94, -61.55) * mm, "mid": v(-91.63, -63.54) * mm, "end": v(-93.75, -64.63) * mm});
            skLineSegment(sketch, "E294.MirrorCS", {"start": v(-92.03, -70.42) * mm, "end": v(-88.91, -68.33) * mm});
            skLineSegment(sketch, "E295.MirrorCS", {"start": v(-84.9, -56.9) * mm, "end": v(-84.57, -55.59) * mm});
            skArc(sketch, "E296.MirrorCS", {"start": v(-92.03, -70.42) * mm, "mid": v(-93.44, -70.12) * mm, "end": v(-93.08, -68.72) * mm});
            skArc(sketch, "E297.MirrorCS", {"start": v(-76.7, -69.13) * mm, "mid": v(-74.7, -68) * mm, "end": v(-75.9, -66.04) * mm});
            skLineSegment(sketch, "E298.MirrorCS", {"start": v(-90.34, -58.33) * mm, "end": v(-88.59, -61.78) * mm});
            skPoint(sketch, "E299.MirrorP", {"position": v(-89.56, -66.39) * mm});
            skArc(sketch, "E300.MirrorCS", {"start": v(-89.06, -72.65) * mm, "mid": v(-87.07, -71.36) * mm, "end": v(-85.98, -73.46) * mm});
            skCircle(sketch, "E301.MirrorC", {"center": v(-85.44, -65.17) * mm, "radius": 8 * mm, "construction": true});
            skArc(sketch, "E302.MirrorCS", {"start": v(-77.13, -65.72) * mm, "mid": v(-79.25, -66.8) * mm, "end": v(-77.95, -68.8) * mm});
            skPoint(sketch, "E303.MirrorP", {"position": v(-82.46, -68.26) * mm});
            skLineSegment(sketch, "E304.MirrorCS", {"start": v(-93.08, -68.72) * mm, "end": v(-89.86, -66.58) * mm});
            skArc(sketch, "E305.MirrorCS", {"start": v(-82.3, -72.99) * mm, "mid": v(-80.99, -73.45) * mm, "end": v(-80.48, -72.16) * mm});
            skArc(sketch, "E306.MirrorCS", {"start": v(-88.6, -57.36) * mm, "mid": v(-89.97, -56.93) * mm, "end": v(-90.34, -58.33) * mm});
            skArc(sketch, "E307.MirrorCS", {"start": v(-81.48, -56.4) * mm, "mid": v(-82.61, -54.44) * mm, "end": v(-84.57, -55.59) * mm});
            skLineSegment(sketch, "E308.MirrorCS", {"start": v(-80.48, -72.16) * mm, "end": v(-82.3, -68.57) * mm});
            skArc(sketch, "E309.MirrorCS", {"start": v(-78.85, -59.93) * mm, "mid": v(-77.49, -60.17) * mm, "end": v(-77.68, -61.54) * mm});
            skPoint(sketch, "E310.MirrorP", {"position": v(-86.73, -61.08) * mm});
            skPoint(sketch, "E311.MirrorP", {"position": v(-93.2, -68.8) * mm});
            skLineSegment(sketch, "E312.MirrorCS", {"start": v(-96.43, -65.17) * mm, "end": v(-73.79, -65.17) * mm, "construction": true});
            skPoint(sketch, "E313.MirrorP", {"position": v(-81.33, -63.96) * mm});
            skLineSegment(sketch, "E314.MirrorCS", {"start": v(-99.15, -61.56) * mm, "end": v(-72.27, -68.65) * mm, "construction": true});
            skPoint(sketch, "E315.MirrorP", {"position": v(-88.43, -62.1) * mm});
            skLineSegment(sketch, "E316.MirrorCS", {"start": v(-85.44, -77.56) * mm, "end": v(-85.44, -52.95) * mm, "construction": true});
            skPoint(sketch, "E317.MirrorP", {"position": v(-84.16, -69.27) * mm});
            skPoint(sketch, "E318.MirrorP", {"position": v(-88.58, -68.1) * mm});
            skPoint(sketch, "E319.MirrorP", {"position": v(-90.4, -58.19) * mm});
            skLineSegment(sketch, "E320.MirrorCS", {"start": v(-81.38, -49.77) * mm, "end": v(-88.78, -77.85) * mm, "construction": true});
            skCircle(sketch, "E321.MirrorC", {"center": v(-85.44, -65.17) * mm, "radius": 9.5 * mm, "construction": true});
            skArc(sketch, "E322.MirrorCS", {"start": v(88.59, -61.78) * mm, "mid": v(88.54, -62.07) * mm, "end": v(88.66, -62.33) * mm});
            skArc(sketch, "E323.MirrorCS", {"start": v(89.64, -66.06) * mm, "mid": v(89.67, -66.35) * mm, "end": v(89.86, -66.58) * mm});
            skArc(sketch, "E324.MirrorCS", {"start": v(89.64, -66.06) * mm, "mid": v(89.6, -64.08) * mm, "end": v(88.66, -62.33) * mm});
            skArc(sketch, "E325.MirrorCS", {"start": v(81.24, -64.29) * mm, "mid": v(81.3, -66.27) * mm, "end": v(82.23, -68.02) * mm});
            skArc(sketch, "E326.MirrorCS", {"start": v(81.24, -64.29) * mm, "mid": v(81.22, -64) * mm, "end": v(81.03, -63.77) * mm});
            skLineSegment(sketch, "E327.MirrorCS", {"start": v(89.06, -72.65) * mm, "end": v(89.4, -73.95) * mm});
            skArc(sketch, "E328.MirrorCS", {"start": v(84.53, -69.37) * mm, "mid": v(84.21, -69.4) * mm, "end": v(83.98, -69.63) * mm});
            skArc(sketch, "E329.MirrorCS", {"start": v(84.9, -56.9) * mm, "mid": v(83.81, -58.99) * mm, "end": v(81.83, -57.7) * mm});
            skArc(sketch, "E330.MirrorCS", {"start": v(88.6, -57.36) * mm, "mid": v(89.97, -56.93) * mm, "end": v(90.34, -58.33) * mm});
            skLineSegment(sketch, "E331.MirrorCS", {"start": v(95, -64.31) * mm, "end": v(93.75, -64.63) * mm});
            skLineSegment(sketch, "E332.MirrorCS", {"start": v(88.6, -57.36) * mm, "end": v(86.9, -60.72) * mm});
            skArc(sketch, "E333.MirrorCS", {"start": v(88.91, -68.33) * mm, "mid": v(88.6, -68.25) * mm, "end": v(88.3, -68.38) * mm});
            skLineSegment(sketch, "E334.MirrorCS", {"start": v(90.34, -58.33) * mm, "end": v(88.59, -61.78) * mm});
            skArc(sketch, "E335.MirrorCS", {"start": v(86.35, -60.98) * mm, "mid": v(84.35, -61.02) * mm, "end": v(82.58, -61.97) * mm});
            skArc(sketch, "E336.MirrorCS", {"start": v(82.3, -68.57) * mm, "mid": v(82.35, -68.28) * mm, "end": v(82.23, -68.02) * mm});
            skLineSegment(sketch, "E337.MirrorCS", {"start": v(84.9, -56.9) * mm, "end": v(84.57, -55.59) * mm});
            skArc(sketch, "E338.MirrorCS", {"start": v(84.53, -69.37) * mm, "mid": v(86.54, -69.33) * mm, "end": v(88.3, -68.38) * mm});
            skArc(sketch, "E339.MirrorCS", {"start": v(86.35, -60.98) * mm, "mid": v(86.68, -60.94) * mm, "end": v(86.9, -60.72) * mm});
            skArc(sketch, "E340.MirrorCS", {"start": v(81.97, -62.02) * mm, "mid": v(82.29, -62.1) * mm, "end": v(82.58, -61.97) * mm});
            skCircle(sketch, "E341.MirrorC", {"center": v(85.44, -65.17) * mm, "radius": 4.3 * mm});
            skPoint(sketch, "E342.MirrorP", {"position": v(89.56, -66.39) * mm});
            skArc(sketch, "E343.MirrorCS", {"start": v(89.06, -72.65) * mm, "mid": v(87.07, -71.36) * mm, "end": v(85.98, -73.46) * mm});
            skArc(sketch, "E344.MirrorCS", {"start": v(82.3, -72.99) * mm, "mid": v(80.99, -73.45) * mm, "end": v(80.48, -72.16) * mm});
            skLineSegment(sketch, "E345.MirrorCS", {"start": v(92.03, -70.42) * mm, "end": v(88.91, -68.33) * mm});
            skLineSegment(sketch, "E346.MirrorCS", {"start": v(85.98, -73.46) * mm, "end": v(86.31, -74.76) * mm});
            skLineSegment(sketch, "E347.MirrorCS", {"start": v(76.7, -69.13) * mm, "end": v(77.95, -68.8) * mm});
            skPoint(sketch, "E348.MirrorP", {"position": v(84.16, -69.27) * mm});
            skArc(sketch, "E349.MirrorCS", {"start": v(77.13, -65.72) * mm, "mid": v(79.25, -66.8) * mm, "end": v(77.95, -68.8) * mm});
            skPoint(sketch, "E350.MirrorP", {"position": v(82.3, -62.24) * mm});
            skLineSegment(sketch, "E351.MirrorCS", {"start": v(81.83, -57.7) * mm, "end": v(81.48, -56.4) * mm});
            skLineSegment(sketch, "E352.MirrorCS", {"start": v(80.48, -72.16) * mm, "end": v(82.3, -68.57) * mm});
            skLineSegment(sketch, "E353.MirrorCS", {"start": v(77.68, -61.54) * mm, "end": v(81.03, -63.77) * mm});
            skLineSegment(sketch, "E354.MirrorCS", {"start": v(93.08, -68.72) * mm, "end": v(89.86, -66.58) * mm});
            skLineSegment(sketch, "E355.MirrorCS", {"start": v(94.18, -61.22) * mm, "end": v(92.94, -61.55) * mm});
            skArc(sketch, "E356.MirrorCS", {"start": v(78.85, -59.93) * mm, "mid": v(77.49, -60.17) * mm, "end": v(77.68, -61.54) * mm});
            skLineSegment(sketch, "E357.MirrorCS", {"start": v(75.9, -66.04) * mm, "end": v(77.13, -65.72) * mm});
            skLineSegment(sketch, "E358.MirrorCS", {"start": v(82.3, -72.99) * mm, "end": v(83.98, -69.63) * mm});
            skLineSegment(sketch, "E359.MirrorCS", {"start": v(78.85, -59.93) * mm, "end": v(81.97, -62.02) * mm});
            skArc(sketch, "E360.MirrorCS", {"start": v(92.03, -70.42) * mm, "mid": v(93.44, -70.12) * mm, "end": v(93.08, -68.72) * mm});
            skPoint(sketch, "E361.MirrorP", {"position": v(88.58, -68.1) * mm});
            skArc(sketch, "E362.MirrorCS", {"start": v(86.31, -74.76) * mm, "mid": v(88.27, -75.9) * mm, "end": v(89.4, -73.95) * mm});
            skPoint(sketch, "E363.MirrorP", {"position": v(81.33, -63.96) * mm});
            skArc(sketch, "E364.MirrorCS", {"start": v(95, -64.31) * mm, "mid": v(96.18, -62.35) * mm, "end": v(94.18, -61.22) * mm});
            skArc(sketch, "E365.MirrorCS", {"start": v(81.48, -56.4) * mm, "mid": v(82.61, -54.44) * mm, "end": v(84.57, -55.59) * mm});
            skLineSegment(sketch, "E366.MirrorCS", {"start": v(96.43, -65.17) * mm, "end": v(73.79, -65.17) * mm, "construction": true});
            skLineSegment(sketch, "E367.MirrorCS", {"start": v(85.44, -77.56) * mm, "end": v(85.44, -52.95) * mm, "construction": true});
            skArc(sketch, "E368.MirrorCS", {"start": v(76.7, -69.13) * mm, "mid": v(74.7, -68) * mm, "end": v(75.9, -66.04) * mm});
            skPoint(sketch, "E369.MirrorP", {"position": v(82.46, -68.26) * mm});
            skPoint(sketch, "E370.MirrorP", {"position": v(90.4, -58.19) * mm});
            skArc(sketch, "E371.MirrorCS", {"start": v(92.94, -61.55) * mm, "mid": v(91.63, -63.54) * mm, "end": v(93.75, -64.63) * mm});
            skPoint(sketch, "E372.MirrorP", {"position": v(88.43, -62.1) * mm});
            skPoint(sketch, "E373.MirrorP", {"position": v(86.73, -61.08) * mm});
            skPoint(sketch, "E374.MirrorP", {"position": v(93.2, -68.8) * mm});
            skCircle(sketch, "E375.MirrorC", {"center": v(85.44, -65.17) * mm, "radius": 9.5 * mm, "construction": true});
            skCircle(sketch, "E376.MirrorC", {"center": v(85.44, -65.17) * mm, "radius": 8 * mm, "construction": true});
            skLineSegment(sketch, "E377.MirrorCS", {"start": v(81.38, -49.77) * mm, "end": v(88.78, -77.85) * mm, "construction": true});
            skLineSegment(sketch, "E378.MirrorCS", {"start": v(99.15, -61.56) * mm, "end": v(72.27, -68.65) * mm, "construction": true});
            skLineSegment(sketch, "E379", {"start": v(-15.2, 33.8) * mm, "end": v(-14.09, 33.8) * mm});
            skLineSegment(sketch, "E380", {"start": v(-13.59, 33.3) * mm, "end": v(-13.59, 33.3) * mm});
            skLineSegment(sketch, "E381", {"start": v(-14.09, 32.8) * mm, "end": v(-14.15, 32.8) * mm});
            skLineSegment(sketch, "E382", {"start": v(-14.15, 32.8) * mm, "end": v(-14.15, 29.76) * mm});
            skLineSegment(sketch, "E383", {"start": v(-14.15, 29.76) * mm, "end": v(-14.09, 29.76) * mm});
            skLineSegment(sketch, "E384", {"start": v(-13.59, 29.26) * mm, "end": v(-13.59, 29.26) * mm});
            skLineSegment(sketch, "E385", {"start": v(-14.09, 28.76) * mm, "end": v(-15.2, 28.76) * mm});
            skLineSegment(sketch, "E386", {"start": v(-15.7, 29.26) * mm, "end": v(-15.7, 29.26) * mm});
            skLineSegment(sketch, "E387", {"start": v(-15.2, 29.76) * mm, "end": v(-15.15, 29.76) * mm});
            skLineSegment(sketch, "E388", {"start": v(-15.15, 29.76) * mm, "end": v(-15.15, 32.8) * mm});
            skLineSegment(sketch, "E389", {"start": v(-15.15, 32.8) * mm, "end": v(-15.21, 32.8) * mm});
            skLineSegment(sketch, "E390", {"start": v(-15.7, 33.3) * mm, "end": v(-15.7, 33.3) * mm});
            skPoint(sketch, "E391.visualSharp", {"position": v(-15.7, 28.76) * mm});
            skArc(sketch, "E391.filletArc", {"start": v(-15.7, 29.26) * mm, "mid": v(-15.56, 28.9) * mm, "end": v(-15.2, 28.76) * mm});
            skPoint(sketch, "E392.visualSharp", {"position": v(-15.7, 29.76) * mm});
            skArc(sketch, "E392.filletArc", {"start": v(-15.2, 29.76) * mm, "mid": v(-15.56, 29.62) * mm, "end": v(-15.7, 29.26) * mm});
            skPoint(sketch, "E393.visualSharp", {"position": v(-13.59, 28.76) * mm});
            skArc(sketch, "E393.filletArc", {"start": v(-14.09, 28.76) * mm, "mid": v(-13.74, 28.9) * mm, "end": v(-13.59, 29.26) * mm});
            skPoint(sketch, "E394.visualSharp", {"position": v(-13.59, 29.76) * mm});
            skArc(sketch, "E394.filletArc", {"start": v(-13.59, 29.26) * mm, "mid": v(-13.74, 29.62) * mm, "end": v(-14.09, 29.76) * mm});
            skPoint(sketch, "E395.visualSharp", {"position": v(-13.59, 32.8) * mm});
            skArc(sketch, "E395.filletArc", {"start": v(-14.09, 32.8) * mm, "mid": v(-13.74, 32.94) * mm, "end": v(-13.6, 33.3) * mm});
            skPoint(sketch, "E396.visualSharp", {"position": v(-13.59, 33.8) * mm});
            skArc(sketch, "E396.filletArc", {"start": v(-13.59, 33.3) * mm, "mid": v(-13.74, 33.65) * mm, "end": v(-14.09, 33.8) * mm});
            skPoint(sketch, "E397.visualSharp", {"position": v(-15.7, 33.8) * mm});
            skArc(sketch, "E397.filletArc", {"start": v(-15.2, 33.8) * mm, "mid": v(-15.56, 33.65) * mm, "end": v(-15.7, 33.3) * mm});
            skPoint(sketch, "E398.visualSharp", {"position": v(-15.71, 32.8) * mm});
            skArc(sketch, "E398.filletArc", {"start": v(-15.71, 33.3) * mm, "mid": v(-15.56, 32.94) * mm, "end": v(-15.21, 32.8) * mm});
            skLineSegment(sketch, "E399.MirrorCS", {"start": v(-14.1, 60.47) * mm, "end": v(-14.15, 60.47) * mm});
            skLineSegment(sketch, "E400.MirrorCS", {"start": v(-14.15, 63.5) * mm, "end": v(-14.1, 63.5) * mm});
            skArc(sketch, "E401.MirrorCS", {"start": v(-14.1, 60.47) * mm, "mid": v(-13.74, 60.32) * mm, "end": v(-13.6, 59.97) * mm});
            skArc(sketch, "E402.MirrorCS", {"start": v(-13.6, 64) * mm, "mid": v(-13.74, 63.65) * mm, "end": v(-14.1, 63.5) * mm});
            skArc(sketch, "E403.MirrorCS", {"start": v(-14.1, 64.5) * mm, "mid": v(-13.74, 64.35) * mm, "end": v(-13.6, 64) * mm});
            skArc(sketch, "E404.MirrorCS", {"start": v(-15.21, 63.5) * mm, "mid": v(-15.56, 63.65) * mm, "end": v(-15.71, 64) * mm});
            skArc(sketch, "E405.MirrorCS", {"start": v(-15.71, 64) * mm, "mid": v(-15.56, 64.35) * mm, "end": v(-15.21, 64.5) * mm});
            skLineSegment(sketch, "E406.MirrorCS", {"start": v(-15.15, 60.47) * mm, "end": v(-15.21, 60.47) * mm});
            skArc(sketch, "E407.MirrorCS", {"start": v(-15.71, 59.97) * mm, "mid": v(-15.56, 60.32) * mm, "end": v(-15.21, 60.47) * mm});
            skLineSegment(sketch, "E408.MirrorCS", {"start": v(-15.21, 59.47) * mm, "end": v(-14.1, 59.47) * mm});
            skArc(sketch, "E409.MirrorCS", {"start": v(-15.21, 59.47) * mm, "mid": v(-15.56, 59.62) * mm, "end": v(-15.71, 59.97) * mm});
            skArc(sketch, "E410.MirrorCS", {"start": v(-13.6, 59.97) * mm, "mid": v(-13.74, 59.62) * mm, "end": v(-14.1, 59.47) * mm});
            skLineSegment(sketch, "E411.MirrorCS", {"start": v(-15.21, 63.5) * mm, "end": v(-15.15, 63.5) * mm});
            skLineSegment(sketch, "E412.MirrorCS", {"start": v(-15.71, 64) * mm, "end": v(-15.71, 64) * mm});
            skPoint(sketch, "E413.MirrorP", {"position": v(-13.6, 63.5) * mm});
            skLineSegment(sketch, "E414.MirrorCS", {"start": v(-14.15, 60.47) * mm, "end": v(-14.15, 63.5) * mm});
            skPoint(sketch, "E415.MirrorP", {"position": v(-13.6, 60.47) * mm});
            skLineSegment(sketch, "E416.MirrorCS", {"start": v(-13.6, 64) * mm, "end": v(-13.6, 64) * mm});
            skLineSegment(sketch, "E417.MirrorCS", {"start": v(-14.1, 64.5) * mm, "end": v(-15.21, 64.5) * mm});
            skLineSegment(sketch, "E418.MirrorCS", {"start": v(-13.6, 59.97) * mm, "end": v(-13.6, 59.97) * mm});
            skPoint(sketch, "E419.MirrorP", {"position": v(-15.71, 60.47) * mm});
            skPoint(sketch, "E420.MirrorP", {"position": v(-13.6, 64.5) * mm});
            skPoint(sketch, "E421.MirrorP", {"position": v(-15.71, 63.5) * mm});
            skLineSegment(sketch, "E422.MirrorCS", {"start": v(-15.71, 59.97) * mm, "end": v(-15.71, 59.97) * mm});
            skPoint(sketch, "E423.MirrorP", {"position": v(-15.71, 59.47) * mm});
            skLineSegment(sketch, "E424.MirrorCS", {"start": v(-15.15, 63.5) * mm, "end": v(-15.15, 60.47) * mm});
            skPoint(sketch, "E425.MirrorP", {"position": v(-13.6, 59.47) * mm});
            skPoint(sketch, "E426.MirrorP", {"position": v(-15.71, 64.5) * mm});
            skLineSegment(sketch, "E427.MirrorCS", {"start": v(15.15, 60.47) * mm, "end": v(15.21, 60.47) * mm});
            skLineSegment(sketch, "E428.MirrorCS", {"start": v(15.21, 63.5) * mm, "end": v(15.15, 63.5) * mm});
            skLineSegment(sketch, "E429.MirrorCS", {"start": v(14.1, 60.47) * mm, "end": v(14.15, 60.47) * mm});
            skLineSegment(sketch, "E430.MirrorCS", {"start": v(14.15, 63.5) * mm, "end": v(14.1, 63.5) * mm});
            skPoint(sketch, "E431.MirrorP", {"position": v(15.71, 63.5) * mm});
            skArc(sketch, "E432.MirrorCS", {"start": v(15.71, 59.97) * mm, "mid": v(15.56, 60.32) * mm, "end": v(15.21, 60.47) * mm});
            skPoint(sketch, "E433.MirrorP", {"position": v(13.6, 64.5) * mm});
            skLineSegment(sketch, "E434.MirrorCS", {"start": v(15.71, 59.97) * mm, "end": v(15.71, 59.97) * mm});
            skPoint(sketch, "E435.MirrorP", {"position": v(15.71, 64.5) * mm});
            skPoint(sketch, "E436.MirrorP", {"position": v(13.6, 63.5) * mm});
            skLineSegment(sketch, "E437.MirrorCS", {"start": v(13.6, 59.97) * mm, "end": v(13.6, 59.97) * mm});
            skArc(sketch, "E438.MirrorCS", {"start": v(15.21, 59.47) * mm, "mid": v(15.56, 59.62) * mm, "end": v(15.71, 59.97) * mm});
            skArc(sketch, "E439.MirrorCS", {"start": v(13.6, 59.97) * mm, "mid": v(13.74, 59.62) * mm, "end": v(14.1, 59.47) * mm});
            skLineSegment(sketch, "E440.MirrorCS", {"start": v(14.15, 60.47) * mm, "end": v(14.15, 63.5) * mm});
            skLineSegment(sketch, "E441.MirrorCS", {"start": v(14.1, 64.5) * mm, "end": v(15.21, 64.5) * mm});
            skLineSegment(sketch, "E442.MirrorCS", {"start": v(15.15, 63.5) * mm, "end": v(15.15, 60.47) * mm});
            skArc(sketch, "E443.MirrorCS", {"start": v(14.1, 60.47) * mm, "mid": v(13.74, 60.32) * mm, "end": v(13.6, 59.97) * mm});
            skPoint(sketch, "E444.MirrorP", {"position": v(15.71, 59.47) * mm});
            skArc(sketch, "E445.MirrorCS", {"start": v(13.6, 64) * mm, "mid": v(13.74, 63.65) * mm, "end": v(14.1, 63.5) * mm});
            skPoint(sketch, "E446.MirrorP", {"position": v(13.6, 60.47) * mm});
            skLineSegment(sketch, "E447.MirrorCS", {"start": v(13.6, 64) * mm, "end": v(13.6, 64) * mm});
            skLineSegment(sketch, "E448.MirrorCS", {"start": v(15.71, 64) * mm, "end": v(15.71, 64) * mm});
            skArc(sketch, "E449.MirrorCS", {"start": v(14.1, 64.5) * mm, "mid": v(13.74, 64.35) * mm, "end": v(13.6, 64) * mm});
            skPoint(sketch, "E450.MirrorP", {"position": v(13.6, 59.47) * mm});
            skArc(sketch, "E451.MirrorCS", {"start": v(15.71, 64) * mm, "mid": v(15.56, 64.35) * mm, "end": v(15.21, 64.5) * mm});
            skArc(sketch, "E452.MirrorCS", {"start": v(15.21, 63.5) * mm, "mid": v(15.56, 63.65) * mm, "end": v(15.71, 64) * mm});
            skLineSegment(sketch, "E453.MirrorCS", {"start": v(15.21, 59.47) * mm, "end": v(14.1, 59.47) * mm});
            skPoint(sketch, "E454.MirrorP", {"position": v(15.71, 60.47) * mm});
            skArc(sketch, "E455.MirrorCS", {"start": v(14.09, 32.8) * mm, "mid": v(13.74, 32.94) * mm, "end": v(13.6, 33.3) * mm});
            skLineSegment(sketch, "E456.MirrorCS", {"start": v(14.09, 32.8) * mm, "end": v(14.15, 32.8) * mm});
            skLineSegment(sketch, "E457.MirrorCS", {"start": v(15.2, 33.8) * mm, "end": v(14.09, 33.8) * mm});
            skArc(sketch, "E458.MirrorCS", {"start": v(15.71, 33.3) * mm, "mid": v(15.56, 32.94) * mm, "end": v(15.21, 32.8) * mm});
            skArc(sketch, "E459.MirrorCS", {"start": v(15.2, 33.8) * mm, "mid": v(15.56, 33.65) * mm, "end": v(15.7, 33.3) * mm});
            skLineSegment(sketch, "E460.MirrorCS", {"start": v(14.09, 28.76) * mm, "end": v(15.2, 28.76) * mm});
            skArc(sketch, "E461.MirrorCS", {"start": v(13.59, 33.3) * mm, "mid": v(13.74, 33.65) * mm, "end": v(14.09, 33.8) * mm});
            skArc(sketch, "E462.MirrorCS", {"start": v(13.59, 29.26) * mm, "mid": v(13.74, 29.62) * mm, "end": v(14.09, 29.76) * mm});
            skArc(sketch, "E463.MirrorCS", {"start": v(14.09, 28.76) * mm, "mid": v(13.74, 28.9) * mm, "end": v(13.59, 29.26) * mm});
            skArc(sketch, "E464.MirrorCS", {"start": v(15.2, 29.76) * mm, "mid": v(15.56, 29.62) * mm, "end": v(15.7, 29.26) * mm});
            skArc(sketch, "E465.MirrorCS", {"start": v(15.7, 29.26) * mm, "mid": v(15.56, 28.9) * mm, "end": v(15.2, 28.76) * mm});
            skLineSegment(sketch, "E466.MirrorCS", {"start": v(15.2, 29.76) * mm, "end": v(15.15, 29.76) * mm});
            skLineSegment(sketch, "E467.MirrorCS", {"start": v(15.15, 32.8) * mm, "end": v(15.21, 32.8) * mm});
            skLineSegment(sketch, "E468.MirrorCS", {"start": v(14.15, 29.76) * mm, "end": v(14.09, 29.76) * mm});
            skLineSegment(sketch, "E469.MirrorCS", {"start": v(14.15, 32.8) * mm, "end": v(14.15, 29.76) * mm});
            skPoint(sketch, "E470.MirrorP", {"position": v(13.59, 32.8) * mm});
            skPoint(sketch, "E471.MirrorP", {"position": v(15.7, 28.76) * mm});
            skPoint(sketch, "E472.MirrorP", {"position": v(15.7, 33.8) * mm});
            skLineSegment(sketch, "E473.MirrorCS", {"start": v(13.59, 33.3) * mm, "end": v(13.59, 33.3) * mm});
            skLineSegment(sketch, "E474.MirrorCS", {"start": v(15.15, 29.76) * mm, "end": v(15.15, 32.8) * mm});
            skPoint(sketch, "E475.MirrorP", {"position": v(13.59, 33.8) * mm});
            skPoint(sketch, "E476.MirrorP", {"position": v(13.59, 28.76) * mm});
            skPoint(sketch, "E477.MirrorP", {"position": v(15.71, 32.8) * mm});
            skPoint(sketch, "E478.MirrorP", {"position": v(13.59, 29.76) * mm});
            skLineSegment(sketch, "E479.MirrorCS", {"start": v(15.7, 33.3) * mm, "end": v(15.7, 33.3) * mm});
            skLineSegment(sketch, "E480.MirrorCS", {"start": v(15.7, 29.26) * mm, "end": v(15.7, 29.26) * mm});
            skPoint(sketch, "E481.MirrorP", {"position": v(15.7, 29.76) * mm});
            skLineSegment(sketch, "E482.MirrorCS", {"start": v(13.59, 29.26) * mm, "end": v(13.59, 29.26) * mm});
            skSolve(sketch);
        }
        {
            var Q0;
            Q0 = qSketchRegion(id + "F0", true);
            extrude(context, id + "F1", {"entities" : qUnion([Q0]), "depth" : 5 * mm, "offsetDistance" : 25 * mm});
        }
    });
